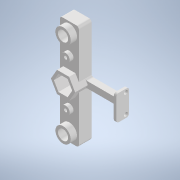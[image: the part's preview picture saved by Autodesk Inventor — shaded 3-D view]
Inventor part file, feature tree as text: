
AUTODESK INVENTOR PART (.ipt)
format: ipt  version: 2022 (Build 260153000, 153)  size: 339,456 bytes
history: native  units: mm
features: reference x9, extrude x7, sketch x6, projected_geometry x6, other x5, fillet x2
ambient origin geometry x8: Origin, YZ Plane, XZ Plane, XY Plane, X Axis, Y Axis, Z Axis, Center Point
bodies: Solid1 (feature_tree)
feature tree (35):
  extrude  "Extrusion1"  Depth=12.5mm
  sketch  "Sketch2"  dims[d2=16.0mm d3=2.0mm]
  extrude  "Extrusion2"  Depth=2.0mm
  extrude  "Extrusion4"  Depth=5.0mm TaperAngle=0.0deg
  extrude  "Extrusion5"  Depth=2.0mm
  extrude  "Extrusion6"  Depth=2.0mm
  extrude  "Extrusion12"  Depth=2.0mm TaperAngle=0.0deg
  fillet  "Fillet2"  Radius=5.0mm
  extrude  "Extrusion19"  Depth=27.5mm TaperAngle=0.0deg
  fillet  "Fillet5"  Radius=32.5mm
  sketch  "Sketch1"  dims[d0=12.5mm d1=80.0mm]
  reference  "Reference1"
  reference  "Reference2"
  reference  "Reference3"
  reference  "Reference4"
  reference  "Reference5"
  reference  "Reference6"
  projected_geometry  "Projected Loop1"
  reference  "Reference7"
  sketch  "Sketch5"  dims[d4=10.0mm d5=0.0mm d6=5.0mm d7=0.0mm]
  reference  "Reference8"
  reference  "Reference9"
  sketch  "Sketch6"  dims[d11=2.0mm d12=2.0mm]
  projected_geometry  "Projected Loop5"
  projected_geometry  "Projected Loop6"
  projected_geometry  "Projected Loop7"
  projected_geometry  "Projected Loop8"
  sketch  "Sketch12"  dims[d13=2.5mm d14=2.0mm]
  sketch  "Sketch21"  dims[d15=3.0mm d16=0.0mm d17=2.0mm d18=0.0mm d19=5.0mm d20=27.5mm d21=0.0mm d42=32.5mm d43=0.0mm d53=2.0mm d84=20.0mm d85=15.0mm d86=3.0mm d87=3.0mm d88=5.0mm d89=5.0mm d90=2.0mm d91=0.0mm d92=2.0mm d40=0.5mm d41=0.872665mm d44=0.5mm d45=0.872665mm]
  projected_geometry  "Projected Loop21"
  other  "<userpath>\OneDrive\Namizje\school\3. letnik\ZOPp\laserski merilnik\3d model\Assembly1.iam"
  other  "Assembly1.iam"
  other  "constraining plate:1"
  other  "spirale:2"
  other  "Hold of motors:1"
